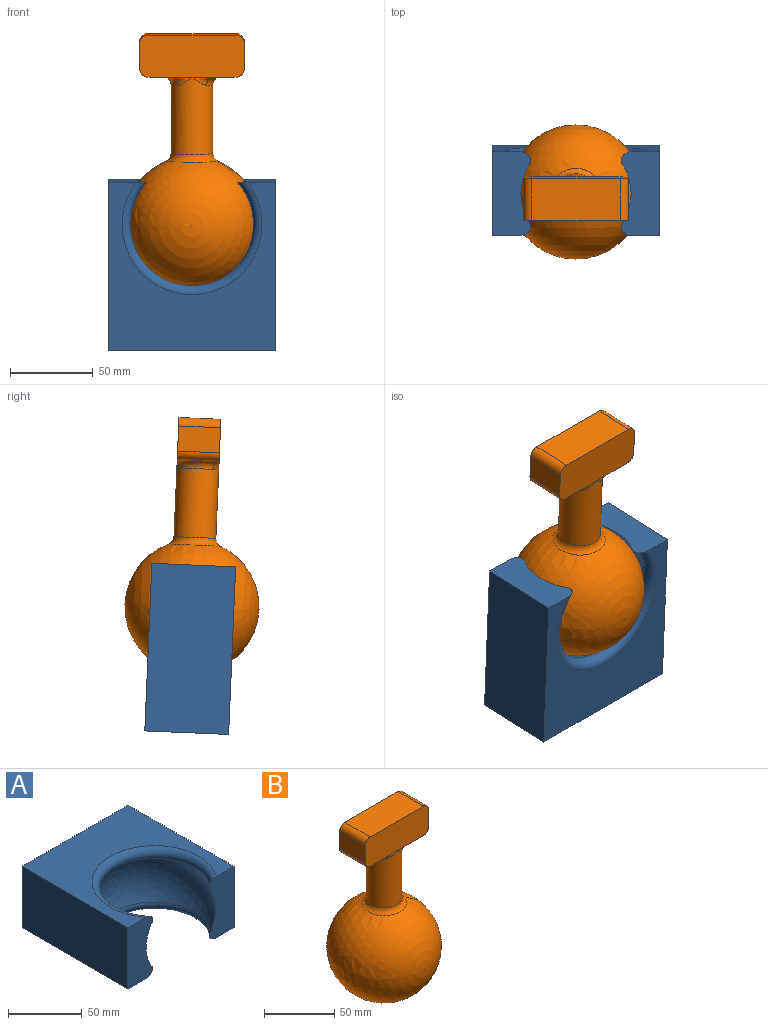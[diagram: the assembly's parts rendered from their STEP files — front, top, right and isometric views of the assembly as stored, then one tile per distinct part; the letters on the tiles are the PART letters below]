
ASSEMBLY  parts=2 mates=1
PART A: 10 faces, bbox 101.6x110.1x83.8 mm
  f0: plane 50.8x23.46mm, normal (0,-1,0), area 1019.9mm2, adj f3,f5,f6,f7,f8,f9
  f1: plane 101.6x50.8mm, normal (1,0,0), area 5161.3mm2, adj f2,f4,f5,f6
  f2: plane 101.6x50.8mm, normal (0,1,0), area 5161.3mm2, adj f1,f3,f5,f6
  f3: plane 101.6x50.8mm, normal (-1,0,0), area 5161.3mm2, adj f0,f2,f5,f6
  f4: plane 50.8x23.46mm, normal (0,-1,0), area 1019.9mm2, adj f1,f5,f6,f7,f8,f9
  f5: plane 101.6x101.6mm, normal (0,0,1), area 5490.3mm2, adj f0,f1,f2,f3,f4,f8
  f6: plane 101.6x101.6mm, normal (0,0,-1), area 5490.3mm2, adj f0,f1,f2,f3,f4,f9
  f7: sphere r=41.91mm, area 6827mm2, adj f0,f4,f8,f9
  f8: torus R=42.37mm, axis (0,0,1), area 1815.4mm2, adj f0,f4,f5,f7
  f9: torus R=42.37mm, axis (0,0,1), area 1815.4mm2, adj f0,f4,f6,f7
PART B: 20 faces, bbox 81.8x81.8x155.5 mm
  f0: cylinder r=12.7mm len=46.78mm, axis (0,0,-1), area 3404.3mm2, adj f9,f10,f11,f16,f17,f18,f19
  f1: sphere r=40.64mm, area 19937.8mm2, adj f16
  f2: plane 25.4x14.23mm, normal (0,0,-1), area 267.9mm2, adj f4,f6,f13,f18
  f3: plane 25.4x14.23mm, normal (0,0,-1), area 267.9mm2, adj f4,f6,f10,f12
  f4: plane 64.04x25.94mm, normal (0,1,0), area 1590.7mm2, adj f2,f3,f5,f7,f8,f9,f12,f13
  f5: plane 25.4x15.24mm, normal (-1,0,0), area 387.1mm2, adj f4,f6,f13,f15
  f6: plane 64.04x25.94mm, normal (0,-1,0), area 1590.7mm2, adj f2,f3,f5,f7,f8,f11,f12,f13
  f7: plane 25.4x15.24mm, normal (1,0,0), area 387.1mm2, adj f4,f6,f12,f14
  f8: plane 53.34x25.4mm, normal (0,0,1), area 1354.8mm2, adj f4,f6,f14,f15
  f9: bspline ~12.82x5.32mm, area 39.3mm2, adj f0,f4,f10
  f10: torus R=17.78mm, axis (0,0,1), area 184.7mm2, adj f0,f3,f9,f11
  f11: bspline ~12.82x5.32mm, area 39.3mm2, adj f0,f6,f10
  f12: cylinder r=5.08mm len=25.4mm, axis (0,1,0), area 202.7mm2, adj f3,f4,f6,f7
  f13: cylinder r=5.08mm len=25.4mm, axis (0,-1,0), area 202.7mm2, adj f2,f4,f5,f6
  f14: cylinder r=5.08mm len=25.4mm, axis (0,-1,0), area 202.7mm2, adj f4,f6,f7,f8
  f15: cylinder r=5.08mm len=25.4mm, axis (0,1,0), area 202.7mm2, adj f4,f5,f6,f8
  f16: torus R=17.78mm, axis (0,0,-1), area 515.4mm2, adj f0,f1
  f17: bspline ~12.82x5.32mm, area 39.3mm2, adj f0,f6,f18
  f18: torus R=17.78mm, axis (0,0,1), area 184.7mm2, adj f0,f2,f17,f19
  f19: bspline ~12.82x5.32mm, area 39.3mm2, adj f0,f4,f18
PLACE A rot(axis=(-1,0,0),87.6deg) t=(128.07,-263.29,-237.92)mm
PLACE B rot(axis=(1,0,0),2.4deg) t=(128.07,-238.98,-211.43)mm
MATE ball A.f8 <-> B.f0  axis (0,1,0.04) through (128.07,-238.98,-211.43)mm
